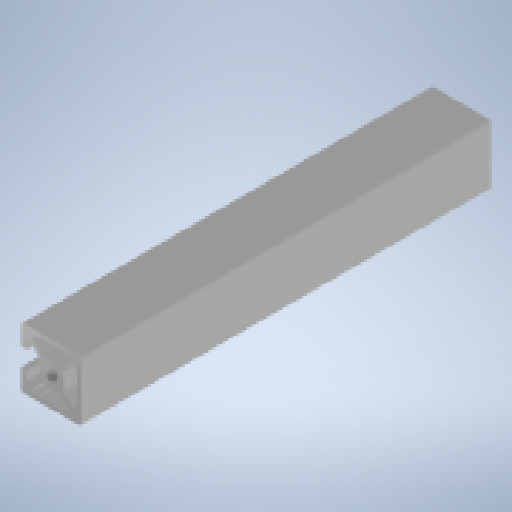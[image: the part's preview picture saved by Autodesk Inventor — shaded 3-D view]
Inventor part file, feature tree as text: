
AUTODESK INVENTOR PART (.ipt)
format: ipt  version: 2024 (Build 280153000, 153)  size: 334,336 bytes
history: native  units: mm
features: other x7, sketch x3, hole x2, thread x2, extrude x1
ambient origin geometry x8: Origin, YZ Plane, XZ Plane, XY Plane, X Axis, Y Axis, Z Axis, Center Point
bodies: Solid1 (feature_tree)
feature tree (15):
  extrude  "Extrusion1"  TaperAngle=0.0deg  [1 undecoded]
  hole  "Hole1"  [1 undecoded]
  other  "C1_XY"
  other  "C1_YZ"
  other  "C1_ZX"
  other  "C1_X"
  other  "C1_Y"
  other  "C1_Z"
  other  "C1_Center"
  thread  "Thread1"  [1 undecoded]
  thread  "Thread2"  [1 undecoded]
  hole  "Hole2"  [1 undecoded]
  sketch  "Sketch_66"  dims[d10=10.0mm d11=0.0mm d12=10.0mm d13=0.0mm d14=5.3mm d15=6.0mm d16=4.0mm d17=2.0mm d18=90.0deg d19=8.0mm d20=20.594885mm]
  sketch  "Sketch2"  dims[d0=135.2mm d1=0.0mm]
  sketch  "Sketch3"  dims[d2=4.2mm d3=6.0mm d4=4.0mm d5=2.0mm d6=90.0deg d7=138.0mm d8=0.0mm d9=0.0mm]
note: 5 required parameter values undecoded (feature->parameter linkage not recoverable at this tier; creation-order binding heuristic only, values carry confidence <= 0.55)
